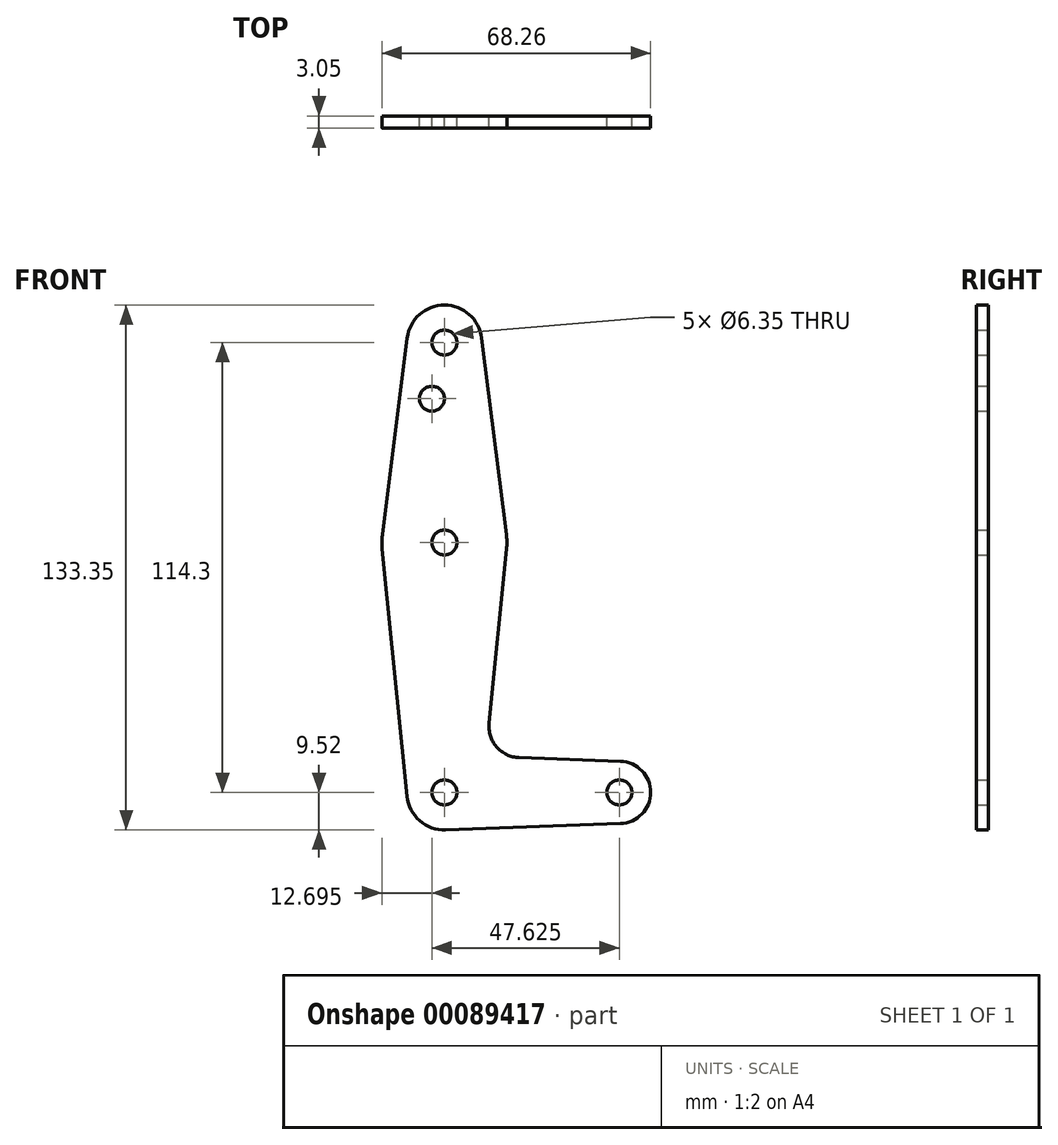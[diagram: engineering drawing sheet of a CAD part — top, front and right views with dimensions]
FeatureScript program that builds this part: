
annotation { "Feature Type Name" : "Feature", "Feature Type Description" : "" }
export const myFeature = defineFeature(function(context is Context, id is Id, definition is map)
    precondition{}
    {
        {
            var Q0;
            Q0=qCreatedBy(makeId("Front.planeOp"),FACE);
            var sketch = newSketch(context, id + "F0", { "sketchPlane" : qUnion([Q0])});
            skLineSegment(sketch, "E0", {"start": v(0, 0) * mm, "end": v(44.45, 0) * mm, "construction": true});
            skLineSegment(sketch, "E1", {"start": v(0, 0) * mm, "end": v(0, 114.3) * mm, "construction": true});
            skCircle(sketch, "E2", {"center": v(0, 114.3) * mm, "radius": 9.53 * mm});
            skCircle(sketch, "E3", {"center": v(0, 63.5) * mm, "radius": 15.88 * mm});
            skCircle(sketch, "E4", {"center": v(0, 0) * mm, "radius": 9.53 * mm});
            skCircle(sketch, "E5", {"center": v(44.45, 0) * mm, "radius": 7.94 * mm});
            skLineSegment(sketch, "E6", {"start": v(11.34, 17.6) * mm, "end": v(15.8, 61.91) * mm});
            skLineSegment(sketch, "E7", {"start": v(-9.48, -0.95) * mm, "end": v(-15.8, 61.91) * mm});
            skLineSegment(sketch, "E8", {"start": v(9.45, 115.5) * mm, "end": v(15.75, 65.48) * mm});
            skLineSegment(sketch, "E9", {"start": v(-9.45, 115.5) * mm, "end": v(-15.75, 65.48) * mm});
            skCircle(sketch, "E10", {"center": v(0, 114.3) * mm, "radius": 3.18 * mm});
            skCircle(sketch, "E11", {"center": v(0, 63.5) * mm, "radius": 3.18 * mm});
            skCircle(sketch, "E12", {"center": v(0, 0) * mm, "radius": 3.18 * mm});
            skCircle(sketch, "E13", {"center": v(44.45, 0) * mm, "radius": 3.18 * mm});
            skCircle(sketch, "E14", {"center": v(-3.17, 100.03) * mm, "radius": 3.18 * mm});
            skLineSegment(sketch, "E15", {"start": v(0.34, -9.52) * mm, "end": v(44.73, -7.93) * mm});
            skLineSegment(sketch, "E16", {"start": v(18.97, 8.85) * mm, "end": v(44.73, 7.93) * mm});
            skArc(sketch, "E17.filletArc", {"start": v(11.34, 17.6) * mm, "mid": v(13.26, 11.57) * mm, "end": v(18.97, 8.85) * mm});
            skSolve(sketch);
        }
        {
            var Q0;
            Q0 = qSketchRegion(id + "F0", true);
            extrude(context, id + "F1", {"entities" : qUnion([Q0]), "depth" : 3.05 * mm});
        }
    });
